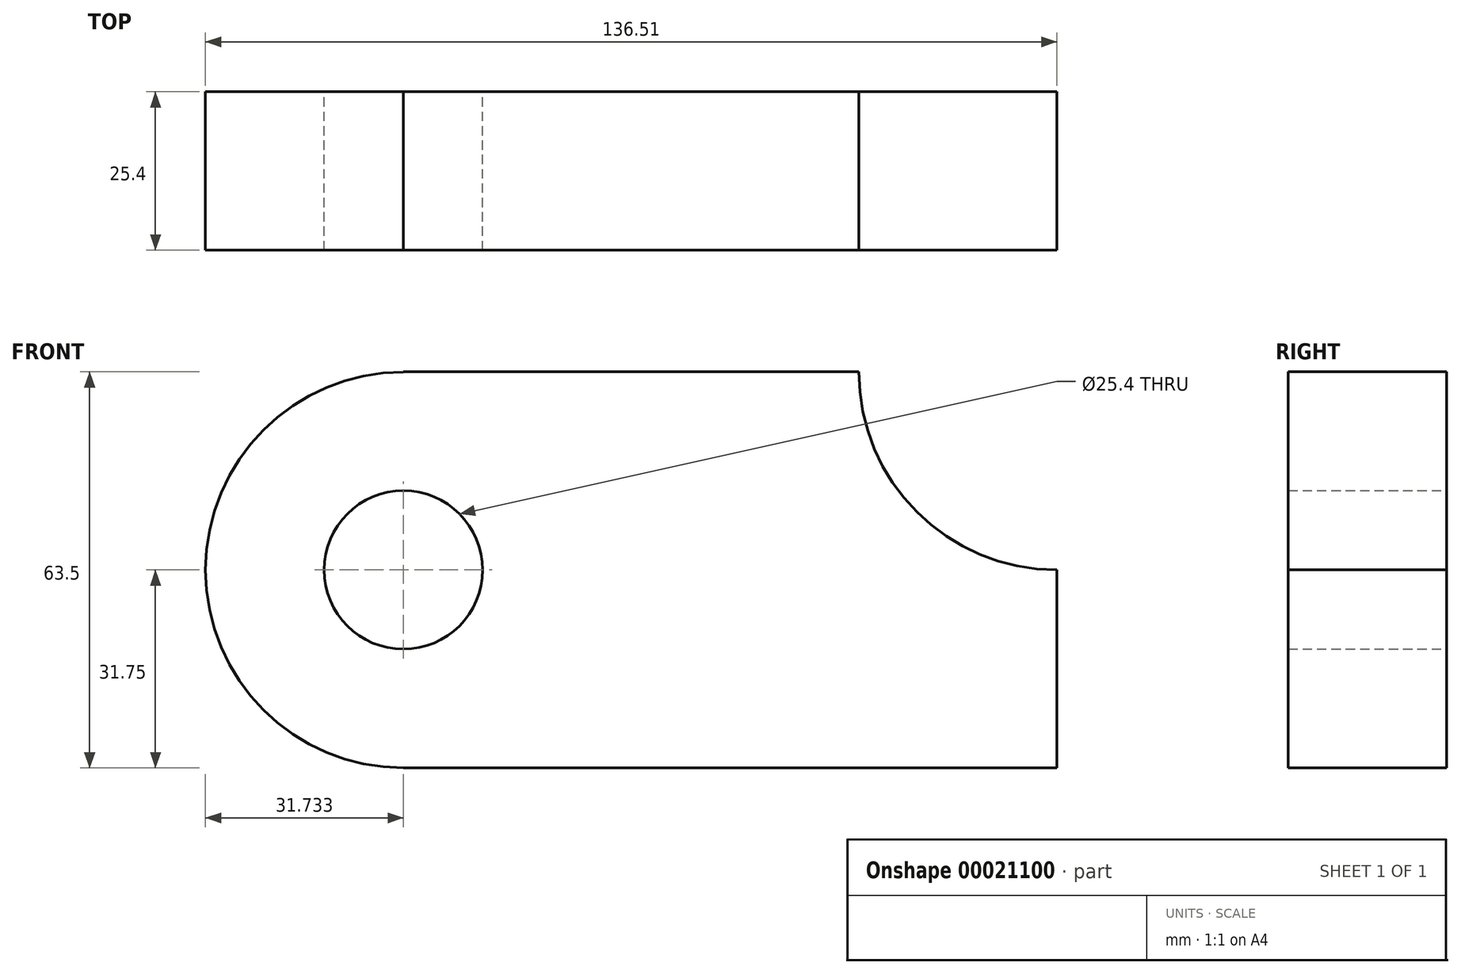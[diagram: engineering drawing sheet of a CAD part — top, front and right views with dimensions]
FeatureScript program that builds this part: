
annotation { "Feature Type Name" : "Feature", "Feature Type Description" : "" }
export const myFeature = defineFeature(function(context is Context, id is Id, definition is map)
    precondition{}
    {
        {
            var Q0;
            Q0=qCreatedBy(makeId("Front.planeOp"),FACE);
            var sketch = newSketch(context, id + "F0", { "sketchPlane" : qUnion([Q0])});
            skLineSegment(sketch, "E0.rect.bottom", {"start": v(-52.39, 31.75) * mm, "end": v(52.39, 31.75) * mm});
            skLineSegment(sketch, "E0.rect.top", {"start": v(-52.39, -31.75) * mm, "end": v(52.39, -31.75) * mm});
            skLineSegment(sketch, "E0.rect.left", {"start": v(-52.39, 31.75) * mm, "end": v(-52.39, -31.75) * mm});
            skLineSegment(sketch, "E0.rect.right", {"start": v(52.39, 31.75) * mm, "end": v(52.39, -31.75) * mm});
            skPoint(sketch, "E0.rect.middle", {"position": v(0, 0) * mm});
            skCircle(sketch, "E1", {"center": v(-52.39, 0) * mm, "radius": 31.73 * mm});
            skCircle(sketch, "E2", {"center": v(-52.39, 0) * mm, "radius": 12.7 * mm});
            skCircle(sketch, "E3", {"center": v(52.39, 31.75) * mm, "radius": 31.75 * mm});
            skSolve(sketch);
        }
        {
            var Q0;
            {var subQ9=sQuery(id+"F0.wireOp",EDGE,"E0.rect.top");Q0=makeQuery(id+"F0.imprint","IMPRINT",FACE,{"disambiguationData":[TD([[makeQuery(id+"F0.imprint","IMPRINT",EDGE,{"derivedFrom":subQ9}),1.0]])]});}
            var Q1;
            {var subQ1=sQuery(id+"F0.wireOp",EDGE,"E0.rect.left");var subQ4=sQuery(id+"F0.wireOp",EDGE,"E1");var subQ6=makeQuery(id+"F0.imprint","INTERSECT",VERTEX,{"disambiguationData":[OD(0.0)],"derivedFrom":[subQ1,subQ4]});Q1=makeQuery(id+"F0.imprint","IMPRINT",FACE,{"disambiguationData":[TD([[makeQuery(id+"F0.imprint","IMPRINT",EDGE,{"disambiguationData":[TD([[subQ6,-1.0]])],"derivedFrom":subQ1}),-1.0]])]});}
            var Q2;
            {var subQ1=sQuery(id+"F0.wireOp",EDGE,"E0.rect.left");var subQ4=sQuery(id+"F0.wireOp",EDGE,"E1");var subQ6=makeQuery(id+"F0.imprint","INTERSECT",VERTEX,{"disambiguationData":[OD(0.0)],"derivedFrom":[subQ1,subQ4]});Q2=makeQuery(id+"F0.imprint","IMPRINT",FACE,{"disambiguationData":[TD([[makeQuery(id+"F0.imprint","IMPRINT",EDGE,{"disambiguationData":[TD([[subQ6,-1.0]])],"derivedFrom":subQ1}),1.0]])]});}
            extrude(context, id + "F1", {"entities" : qUnion([Q0, Q1, Q2]), "depth" : 25.4 * mm});
        }
    });
